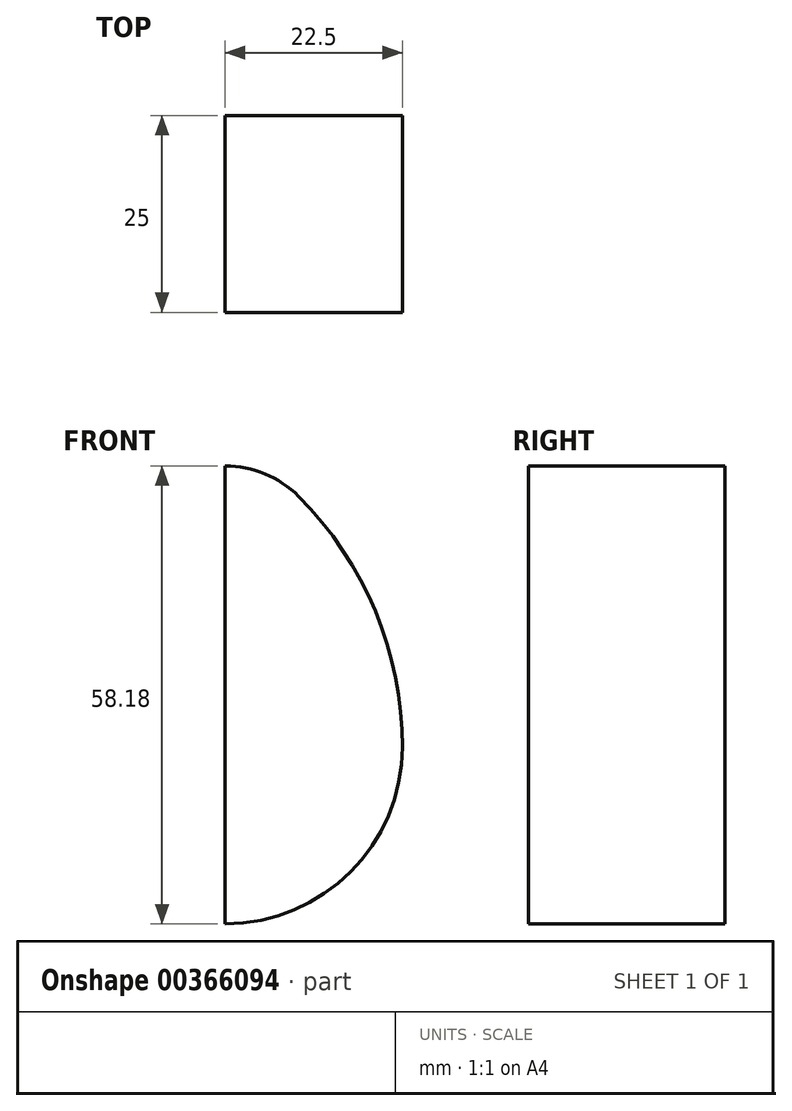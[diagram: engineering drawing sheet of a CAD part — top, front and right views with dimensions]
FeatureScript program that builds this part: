
annotation { "Feature Type Name" : "Feature", "Feature Type Description" : "" }
export const myFeature = defineFeature(function(context is Context, id is Id, definition is map)
    precondition{}
    {
        {
            var Q0;
            Q0=qCreatedBy(makeId("Front.planeOp"),FACE);
            var sketch = newSketch(context, id + "F0", { "sketchPlane" : qUnion([Q0])});
            skArc(sketch, "E0", {"start": v(0, -22.5) * mm, "mid": v(15.9, -15.9) * mm, "end": v(22.5, 0) * mm});
            skArc(sketch, "E1", {"start": v(22.5, 0) * mm, "mid": v(19.07, 17.22) * mm, "end": v(9.32, 31.82) * mm});
            skArc(sketch, "E2", {"start": v(9.32, 31.82) * mm, "mid": v(5.04, 34.68) * mm, "end": v(0, 35.68) * mm});
            skLineSegment(sketch, "E3", {"start": v(0, 35.68) * mm, "end": v(0, -22.5) * mm});
            skLineSegment(sketch, "E4", {"start": v(0, -22.5) * mm, "end": v(0, 35.68) * mm});
            skSolve(sketch);
        }
        {
            var Q0;
            Q0 = qSketchRegion(id + "F0", true);
            extrude(context, id + "F1", {"entities" : qUnion([Q0]), "depth" : 25 * mm});
        }
    });
